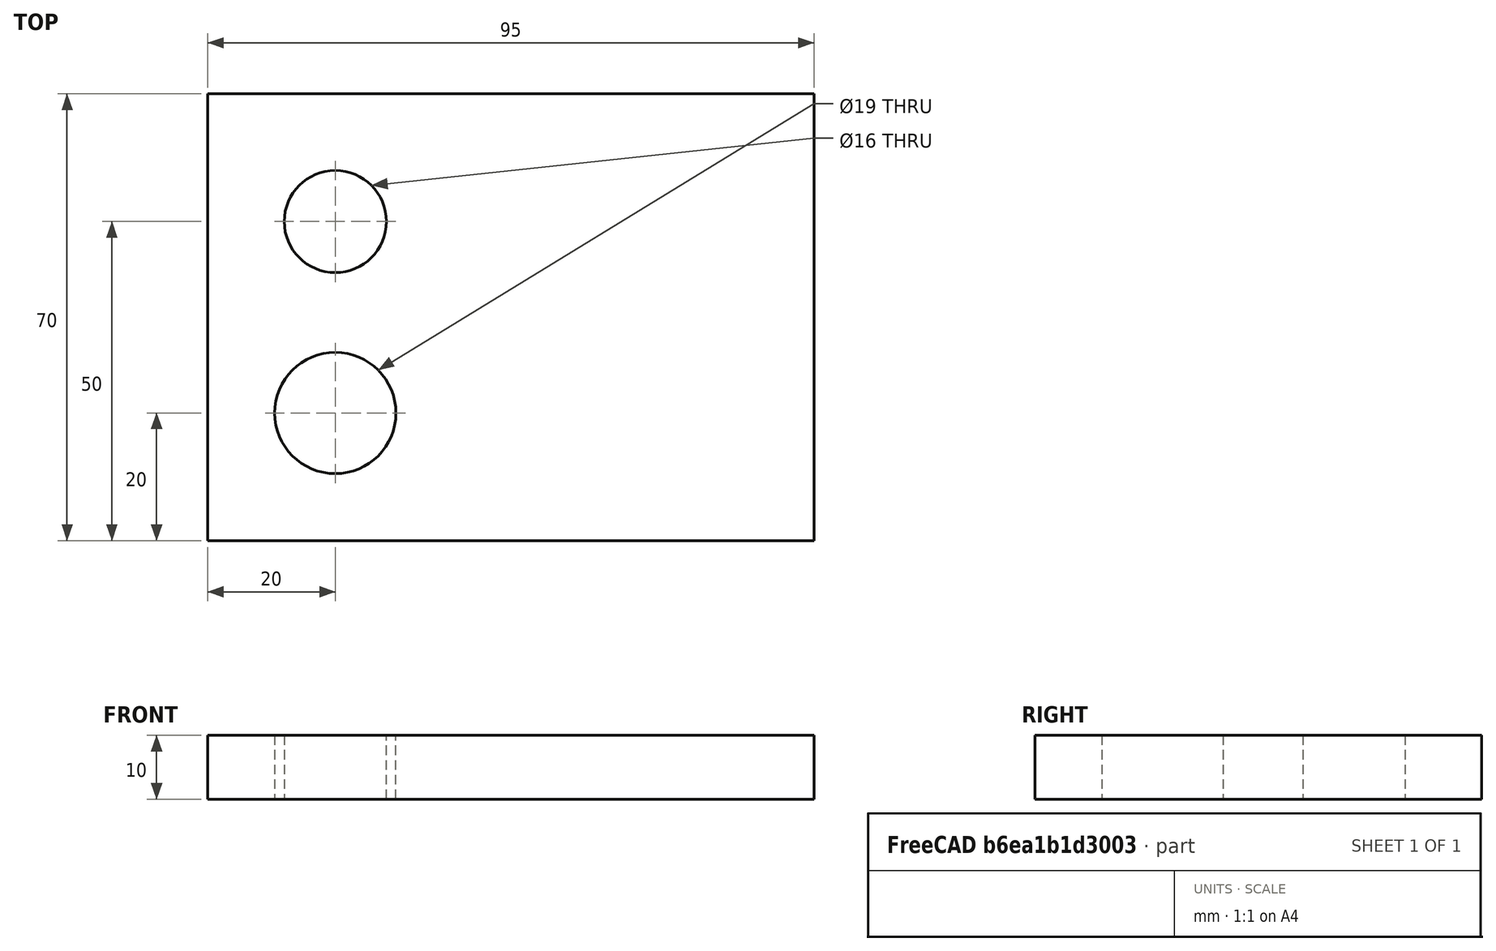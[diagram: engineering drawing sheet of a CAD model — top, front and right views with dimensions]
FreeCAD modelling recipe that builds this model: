
FCSTD DOCUMENT  (FreeCAD 0.19R24276 (Git))
Label: BLDC_holder_part2_middle
License: All rights reserved
LicenseURL: http://en.wikipedia.org/wiki/All_rights_reserved
objects: Sketcher::SketchObject×1, PartDesign::Pad×1, PartDesign::Body×1
note: 4 computed .brp shape members not serialized (recipe doc carries the construction recipe); baked Part::Feature solids carry a one-line shape summary decoded from their .brp

FEATURE [Sketcher::SketchObject] Sketch  label="Sketch_D16_D19_L70X75"
  FullyConstrained = true
  MapMode = 5
  Support = -> [XY_Plane]
  sketch-geometry (6):
    g0: Circle CenterX=0 CenterY=0 CenterZ=0 NormalX=0 NormalY=0 NormalZ=1 AngleXU=0 Radius=8
    g1: Circle CenterX=0 CenterY=-30 CenterZ=0 NormalX=0 NormalY=0 NormalZ=1 AngleXU=0 Radius=9.5
    g2: LineSegment StartX=-20 StartY=20 StartZ=0 EndX=75 EndY=20 EndZ=0
    g3: LineSegment StartX=75 StartY=20 StartZ=0 EndX=75 EndY=-50 EndZ=0
    g4: LineSegment StartX=75 StartY=-50 StartZ=0 EndX=-20 EndY=-50 EndZ=0
    g5: LineSegment StartX=-20 StartY=-50 StartZ=0 EndX=-20 EndY=20 EndZ=0
  constraints (17):
    c: Coincident(g0,g-1)
    c: Diameter(g0) = 16
    c: PointOnObject(g1,g-2)
    c: Diameter(g1) = 19
    c: DistanceY(g1,g0) = 30
    c: Coincident(g2,g3)
    c: Coincident(g3,g4)
    c: Coincident(g4,g5)
    c: Coincident(g5,g2)
    c: Horizontal(g2)
    c: Horizontal(g4)
    c: Vertical(g3)
    c: Vertical(g5)
    c: DistanceX(g0,g2) = 75
    c: DistanceY(g4,g1) = 20
    c: DistanceX(g2,g0) = 20
    c: DistanceY(g3,g2) = 70
FEATURE [PartDesign::Pad] Pad  label="Pad_h10"
  Direction = (1,1,1)
  Length = 10
  Length2 = 100
  Profile = -> Sketch
  Type = 0
FEATURE [PartDesign::Body] Body
  Group = -> [Sketch,Pad]
  Origin = -> Origin
  Tip = -> Pad
